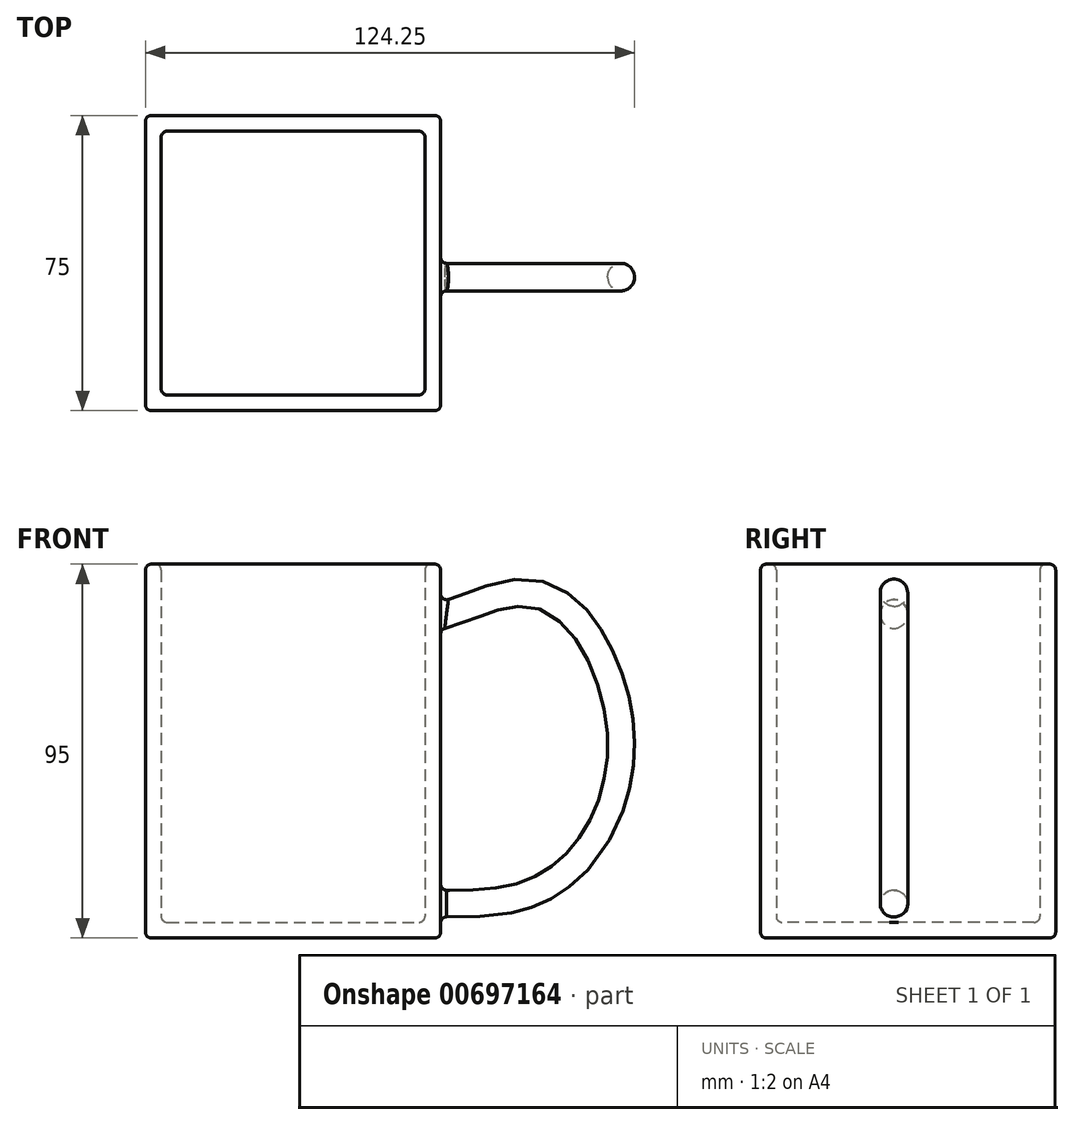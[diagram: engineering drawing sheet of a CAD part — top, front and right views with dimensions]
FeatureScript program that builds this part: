
annotation { "Feature Type Name" : "Feature", "Feature Type Description" : "" }
export const myFeature = defineFeature(function(context is Context, id is Id, definition is map)
    precondition{}
    {
        {
            var Q0;
            Q0=qCreatedBy(makeId("Top.planeOp"),FACE);
            var sketch = newSketch(context, id + "F0", { "sketchPlane" : qUnion([Q0])});
            skLineSegment(sketch, "E0.bottom", {"start": v(-42.58, 41.08) * mm, "end": v(32.42, 41.08) * mm});
            skLineSegment(sketch, "E0.top", {"start": v(-42.58, -33.92) * mm, "end": v(32.42, -33.92) * mm});
            skLineSegment(sketch, "E0.left", {"start": v(-42.58, 41.08) * mm, "end": v(-42.58, -33.92) * mm});
            skLineSegment(sketch, "E0.right", {"start": v(32.42, 41.08) * mm, "end": v(32.42, -33.92) * mm});
            skSolve(sketch);
        }
        {
            var Q0;
            Q0 = qSketchRegion(id + "F0", true);
            extrude(context, id + "F1", {"entities" : qUnion([Q0]), "depth" : 95 * mm, "offsetDistance" : 25 * mm});
        }
        {
            var Q0;
            Q0=qCreatedBy(makeId("Front.planeOp"),FACE);
            var sketch = newSketch(context, id + "F2", { "sketchPlane" : qUnion([Q0])});
            skFitSpline(sketch, "E1", {"points": [v(22.47, 71.24) * mm, v(41.64, 77) * mm, v(56.77, 79.33) * mm, v(69.33, 59.52) * mm, v(68.48, 36.3) * mm, v(58.68, 22.03) * mm, v(42.28, 16.5) * mm, v(22.47, 17.35) * mm, v(22.26, 17.56) * mm, v(22.26, 17.77) * mm], "startDerivative": vector(138.73, 37.5) * mm, "endDerivative": vector(0.97, 15.28) * mm});
            skSolve(sketch);
        }
        {
            var Q0;
            Q0=qCreatedBy(makeId("Right.planeOp"),FACE);
            cPlane(context, id + "F3", {"entities" : qUnion([Q0]), "cplaneType" : CPlaneType.OFFSET, "offset" : 25 * mm, "width" : 150 * mm, "height" : 150 * mm});
        }
        {
            var Q0;
            Q0=qCreatedBy(id+"F3.planeOp",FACE);
            var sketch = newSketch(context, id + "F4", { "sketchPlane" : qUnion([Q0])});
            skCircle(sketch, "E2", {"center": v(0, 79.76) * mm, "radius": 3.5 * mm});
            skSolve(sketch);
        }
        {
            var Q0;
            Q0 = qSketchRegion(id + "F4", true);
            var Q1;
            Q1 = qConstructionFilter(qBodyType(qCreatedBy(id + "F2" ,EDGE), BodyType.WIRE), ConstructionObject.NO);
            sweep(context, id + "F5", {"operationType" : NewBodyOperationType.ADD, "profiles" : qUnion([Q0]), "path" : qUnion([Q1])});
        }
        {
            var Q0;
            Q0=makeQuery(id+"F1.opExtrude","CAP_FACE",FACE,{"disambiguationData":[OSD([sQuery(id+"F0.wireOp",EDGE,"E0.bottom"),sQuery(id+"F0.wireOp",EDGE,"E0.top"),sQuery(id+"F0.wireOp",EDGE,"E0.left"),sQuery(id+"F0.wireOp",EDGE,"E0.right")])],"isStart":false});
            shell(context, id + "F6", {"entities" : qUnion([Q0]), "thickness" : 4 * mm});
        }
        {
            var Q0;
            Q0=makeQuery(id+"F1.opExtrude","CAP_EDGE",EDGE,{"disambiguationData":[OSD([sQuery(id+"F0.wireOp",EDGE,"E0.left")])],"isStart":false});
            var Q1;
            {var subQ0=sQuery(id+"F0.wireOp",EDGE,"E0.left");Q1=makeQuery(id+"F6.opShell","OFFSET_EDGE",EDGE,{"disambiguationData":[OSD([subQ0]),TDD([makeQuery(id+"F1.opExtrude","CAP_EDGE",EDGE,{"disambiguationData":[OSD([subQ0])],"isStart":false})])]});}
            var Q2;
            Q2=makeQuery(id+"F1.opExtrude","CAP_FACE",FACE,{"disambiguationData":[OSD([sQuery(id+"F0.wireOp",EDGE,"E0.bottom"),sQuery(id+"F0.wireOp",EDGE,"E0.top"),sQuery(id+"F0.wireOp",EDGE,"E0.left"),sQuery(id+"F0.wireOp",EDGE,"E0.right")])],"isStart":false});
            var Q3;
            Q3=makeQuery(id+"F1.opExtrude","CAP_EDGE",EDGE,{"disambiguationData":[OSD([sQuery(id+"F0.wireOp",EDGE,"E0.top")])],"isStart":false});
            var Q4;
            {var subQ0=sQuery(id+"F0.wireOp",EDGE,"E0.bottom");Q4=makeQuery(id+"F6.opShell","OFFSET_EDGE",EDGE,{"disambiguationData":[OSD([subQ0]),TDD([makeQuery(id+"F1.opExtrude","CAP_EDGE",EDGE,{"disambiguationData":[OSD([subQ0])],"isStart":false})])]});}
            var Q5;
            Q5=makeQuery(id+"F1.opExtrude","CAP_EDGE",EDGE,{"disambiguationData":[OSD([sQuery(id+"F0.wireOp",EDGE,"E0.bottom")])],"isStart":false});
            var Q6;
            Q6=makeQuery(id+"F1.opExtrude","CAP_EDGE",EDGE,{"disambiguationData":[OSD([sQuery(id+"F0.wireOp",EDGE,"E0.right")])],"isStart":false});
            var Q7;
            Q7=makeQuery(id+"F5.boolean.opBoolean","INTERSECT",EDGE,{"disambiguationData":[OD(1.0)],"derivedFrom":[makeQuery(id+"F1.opExtrude","SWEPT_FACE",FACE,{"disambiguationData":[OSD([sQuery(id+"F0.wireOp",EDGE,"E0.right")])]}),makeQuery(id+"F5.opSweep","SWEPT_FACE",FACE,{"disambiguationData":[OSD([sQuery(id+"F2.wireOp",EDGE,"E1"),sQuery(id+"F4.wireOp",EDGE,"E2")])]})]});
            var Q8;
            Q8=makeQuery(id+"F5.boolean.opBoolean","INTERSECT",EDGE,{"disambiguationData":[OD(0.0)],"derivedFrom":[makeQuery(id+"F1.opExtrude","SWEPT_FACE",FACE,{"disambiguationData":[OSD([sQuery(id+"F0.wireOp",EDGE,"E0.right")])]}),makeQuery(id+"F5.opSweep","SWEPT_FACE",FACE,{"disambiguationData":[OSD([sQuery(id+"F2.wireOp",EDGE,"E1"),sQuery(id+"F4.wireOp",EDGE,"E2")])]})]});
            var Q9;
            Q9=makeQuery(id+"F1.opExtrude","SWEPT_EDGE",EDGE,{"disambiguationData":[OSD([sQuery(id+"F0.wireOp",EDGE,"E0.top"),sQuery(id+"F0.wireOp",EDGE,"E0.right")])]});
            var Q10;
            Q10=makeQuery(id+"F1.opExtrude","SWEPT_EDGE",EDGE,{"disambiguationData":[OSD([sQuery(id+"F0.wireOp",EDGE,"E0.top"),sQuery(id+"F0.wireOp",EDGE,"E0.left")])]});
            var Q11;
            Q11=makeQuery(id+"F1.opExtrude","SWEPT_EDGE",EDGE,{"disambiguationData":[OSD([sQuery(id+"F0.wireOp",EDGE,"E0.bottom"),sQuery(id+"F0.wireOp",EDGE,"E0.left")])]});
            var Q12;
            Q12=makeQuery(id+"F1.opExtrude","SWEPT_EDGE",EDGE,{"disambiguationData":[OSD([sQuery(id+"F0.wireOp",EDGE,"E0.bottom"),sQuery(id+"F0.wireOp",EDGE,"E0.right")])]});
            var Q13;
            Q13=makeQuery(id+"F1.opExtrude","CAP_EDGE",EDGE,{"disambiguationData":[OSD([sQuery(id+"F0.wireOp",EDGE,"E0.bottom")])],"isStart":true});
            var Q14;
            Q14=makeQuery(id+"F1.opExtrude","CAP_EDGE",EDGE,{"disambiguationData":[OSD([sQuery(id+"F0.wireOp",EDGE,"E0.left")])],"isStart":true});
            var Q15;
            Q15=makeQuery(id+"F1.opExtrude","CAP_EDGE",EDGE,{"disambiguationData":[OSD([sQuery(id+"F0.wireOp",EDGE,"E0.top")])],"isStart":true});
            var Q16;
            Q16=makeQuery(id+"F1.opExtrude","CAP_EDGE",EDGE,{"disambiguationData":[OSD([sQuery(id+"F0.wireOp",EDGE,"E0.right")])],"isStart":true});
            var Q17;
            Q17=makeQuery(id+"F6.opShell","OFFSET_EDGE",EDGE,{"disambiguationData":[OSD([sQuery(id+"F0.wireOp",EDGE,"E0.top"),sQuery(id+"F0.wireOp",EDGE,"E0.left")])]});
            var Q18;
            Q18=makeQuery(id+"F6.opShell","OFFSET_EDGE",EDGE,{"disambiguationData":[OSD([sQuery(id+"F0.wireOp",EDGE,"E0.bottom"),sQuery(id+"F0.wireOp",EDGE,"E0.left")])]});
            var Q19;
            Q19=makeQuery(id+"F6.opShell","OFFSET_EDGE",EDGE,{"disambiguationData":[OSD([sQuery(id+"F0.wireOp",EDGE,"E0.top"),sQuery(id+"F0.wireOp",EDGE,"E0.right")])]});
            var Q20;
            Q20=makeQuery(id+"F6.opShell","OFFSET_EDGE",EDGE,{"disambiguationData":[OSD([sQuery(id+"F0.wireOp",EDGE,"E0.bottom"),sQuery(id+"F0.wireOp",EDGE,"E0.right")])]});
            var Q21;
            {var subQ0=sQuery(id+"F0.wireOp",EDGE,"E0.left");Q21=makeQuery(id+"F6.opShell","OFFSET_EDGE",EDGE,{"disambiguationData":[OSD([subQ0]),TDD([makeQuery(id+"F1.opExtrude","CAP_EDGE",EDGE,{"disambiguationData":[OSD([subQ0])],"isStart":true})])]});}
            var Q22;
            {var subQ0=sQuery(id+"F0.wireOp",EDGE,"E0.top");Q22=makeQuery(id+"F6.opShell","OFFSET_EDGE",EDGE,{"disambiguationData":[OSD([subQ0]),TDD([makeQuery(id+"F1.opExtrude","CAP_EDGE",EDGE,{"disambiguationData":[OSD([subQ0])],"isStart":true})])]});}
            var Q23;
            {var subQ0=sQuery(id+"F0.wireOp",EDGE,"E0.bottom");Q23=makeQuery(id+"F6.opShell","OFFSET_EDGE",EDGE,{"disambiguationData":[OSD([subQ0]),TDD([makeQuery(id+"F1.opExtrude","CAP_EDGE",EDGE,{"disambiguationData":[OSD([subQ0])],"isStart":true})])]});}
            var Q24;
            {var subQ0=sQuery(id+"F0.wireOp",EDGE,"E0.right");Q24=makeQuery(id+"F6.opShell","OFFSET_EDGE",EDGE,{"disambiguationData":[OSD([subQ0]),TDD([makeQuery(id+"F1.opExtrude","CAP_EDGE",EDGE,{"disambiguationData":[OSD([subQ0])],"isStart":true})])]});}
            fillet(context, id + "F7", {"entities" : qUnion([Q0, Q1, Q2, Q3, Q4, Q5, Q6, Q7, Q8, Q9, Q10, Q11, Q12, Q13, Q14, Q15, Q16, Q17, Q18, Q19, Q20, Q21, Q22, Q23, Q24]), "radius" : 1.5 * mm, "tangentPropagation" : true, "allowEdgeOverflow" : false});
        }
    });
